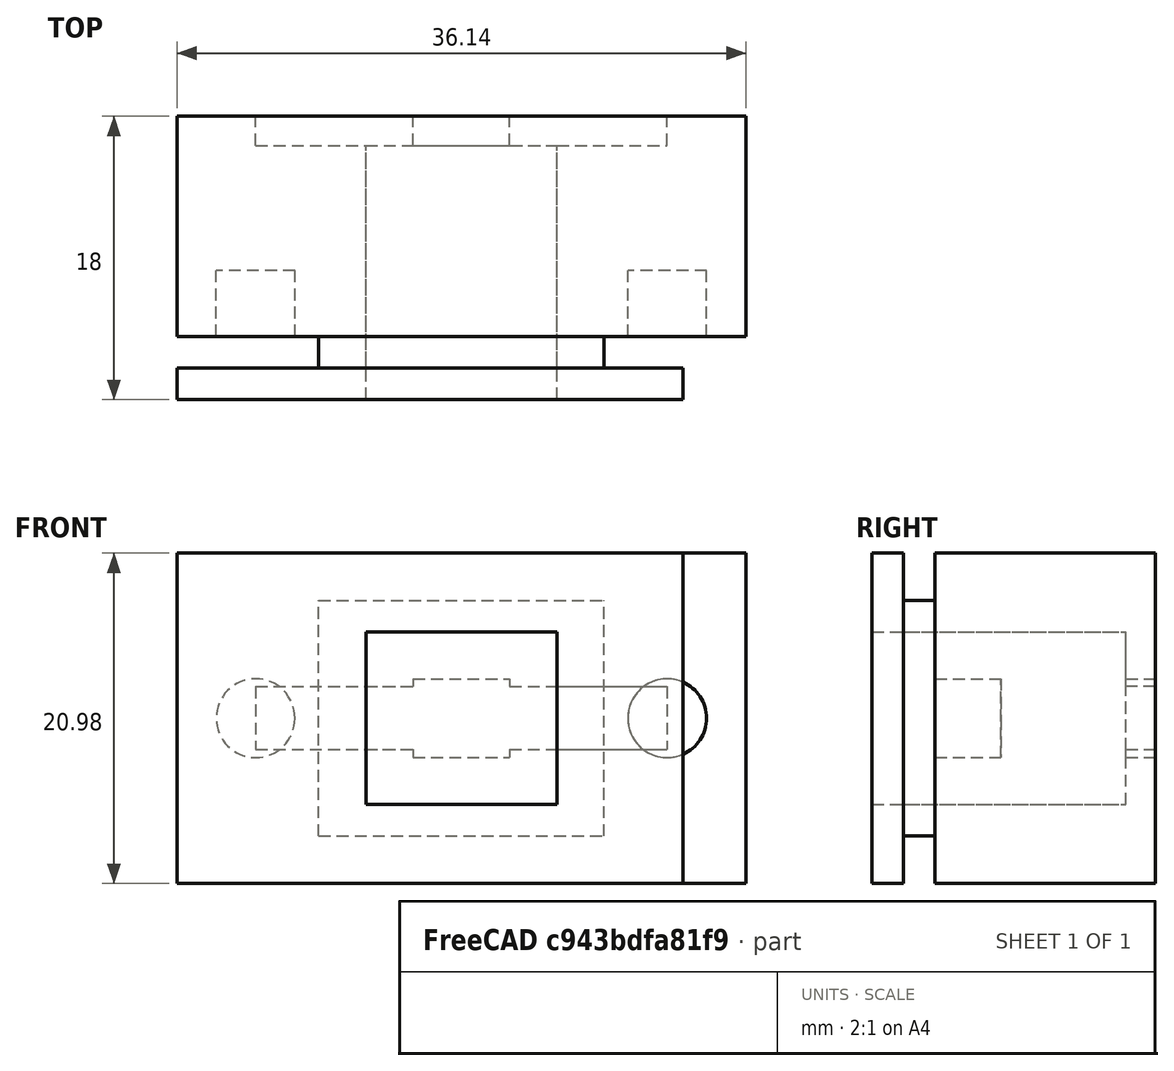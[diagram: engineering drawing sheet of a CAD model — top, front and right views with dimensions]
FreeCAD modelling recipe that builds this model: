
FCSTD DOCUMENT  (FreeCAD 0.18R16117 (Git))
Label: USB_B_Panelmount
License: All rights reserved
LicenseURL: http://en.wikipedia.org/wiki/All_rights_reserved
objects: Part::Box×8, Part::Cut×5, Part::Cylinder×2
note: 15 computed .brp shape members not serialized (recipe doc carries the construction recipe); baked Part::Feature solids carry a one-line shape summary decoded from their .brp

FEATURE [Part::Box] Box  label="USB"
  AttacherType = Attacher::AttachEngine3D
  Height = 10.98
  Length = 12.14
  Placement = pos=(12,0,5) rot=(0,0,1;0rad)
  Width = 16.14
FEATURE [Part::Box] Box001  label="Panel"
  AttacherType = Attacher::AttachEngine3D
  Height = 20.98
  Length = 32.14
  Width = 2
FEATURE [Part::Box] Box002  label="Cube001"
  AttacherType = Attacher::AttachEngine3D
  Height = 20.98
  Length = 36.14
  Placement = pos=(0,2,0) rot=(0,0,1;0rad)
  Width = 16
FEATURE [Part::Box] Box003  label="Cube002"
  AttacherType = Attacher::AttachEngine3D
  Height = 4.98
  Length = 6.14
  Placement = pos=(15,16.14,8) rot=(0,0,1;0rad)
  Width = 10
FEATURE [Part::Box] Box004  label="Cube003"
  AttacherType = Attacher::AttachEngine3D
  Height = 4
  Length = 26.14
  Placement = pos=(5,16.14,8.5) rot=(0,0,1;0rad)
  Width = 10
FEATURE [Part::Cylinder] Cylinder
  Angle = 360
  AttacherType = Attacher::AttachEngine3D
  Height = 4.2
  Placement = pos=(5,4,10.49) rot=(-1,0,0;1.5708rad)
  Radius = 2.5
FEATURE [Part::Box] Box005  label="Cube004"
  AttacherType = Attacher::AttachEngine3D
  Height = 10.98
  Length = 12.14
  Placement = pos=(12,0,5) rot=(0,0,1;0rad)
  Width = 16.14
FEATURE [Part::Cylinder] Cylinder001
  Angle = 360
  AttacherType = Attacher::AttachEngine3D
  Height = 4.2
  Placement = pos=(31.14,4,10.49) rot=(-1,0,0;1.5708rad)
  Radius = 2.5
FEATURE [Part::Cut] Cut
  Base = -> Box002
  Tool = -> Box005
FEATURE [Part::Cut] Cut001
  Base = -> Cut
  Tool = -> Box003
FEATURE [Part::Cut] Cut002
  Base = -> Cut001
  Tool = -> Box004
FEATURE [Part::Box] Box006  label="Cube"
  AttacherType = Attacher::AttachEngine3D
  Height = 20.98
  Length = 36.14
  Width = 4
FEATURE [Part::Box] Box007  label="Cube005"
  AttacherType = Attacher::AttachEngine3D
  Height = 14.98
  Length = 18.14
  Placement = pos=(9,0,3) rot=(0,0,1;0rad)
  Width = 4
FEATURE [Part::Cut] Cut003
  Base = -> Box006
  Tool = -> Box007
FEATURE [Part::Cut] Cut004
  Base = -> Cut002
  Tool = -> Cut003
